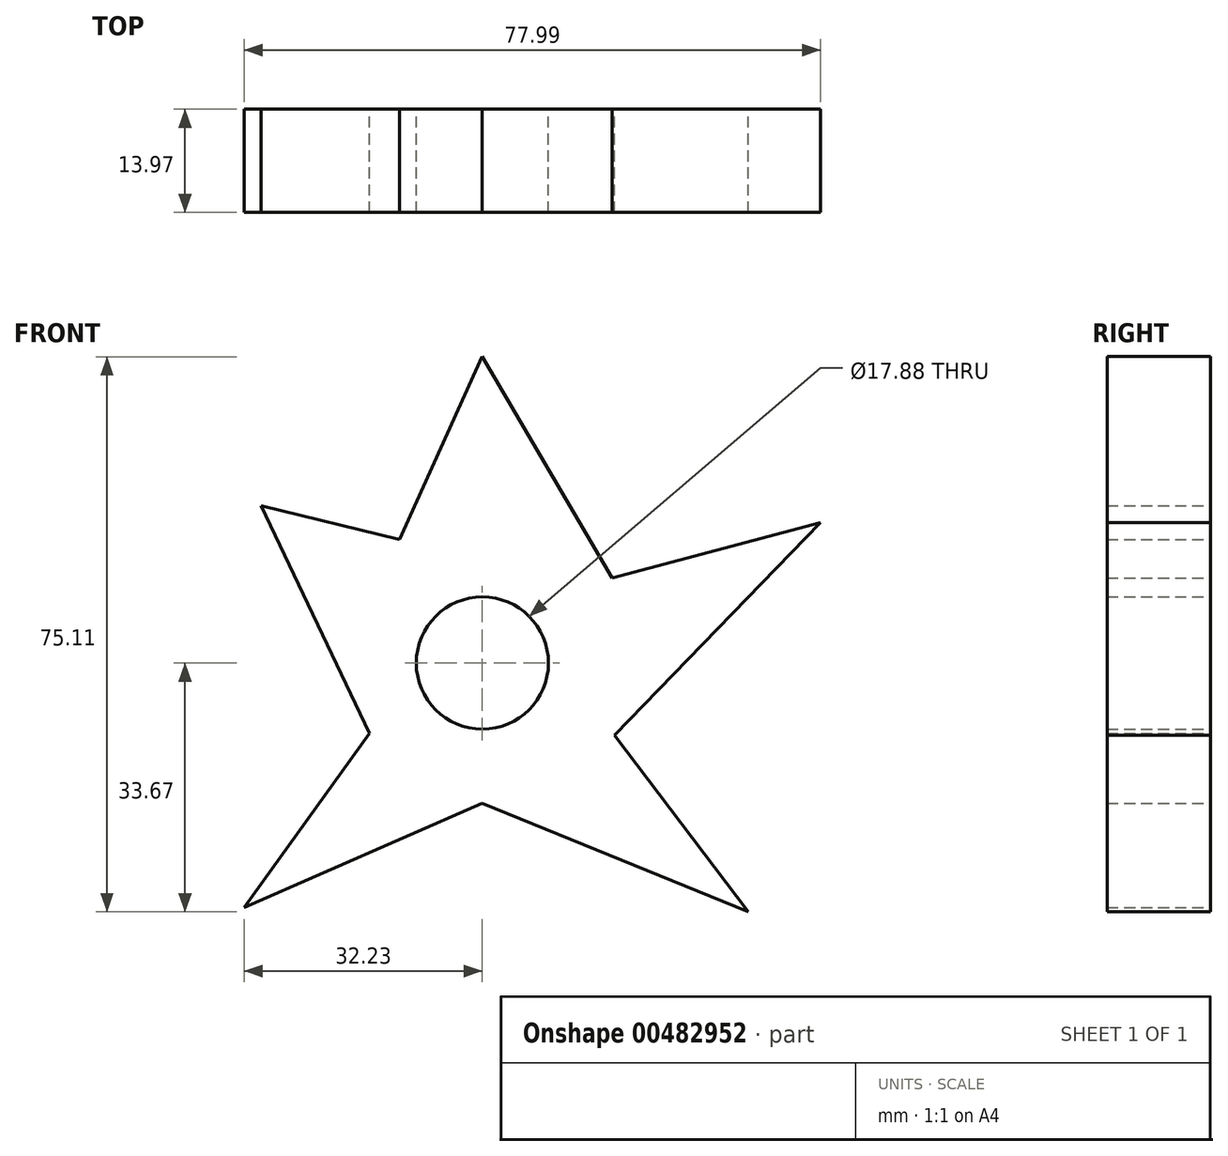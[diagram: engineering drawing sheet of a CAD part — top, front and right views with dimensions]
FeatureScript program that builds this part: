
annotation { "Feature Type Name" : "Feature", "Feature Type Description" : "" }
export const myFeature = defineFeature(function(context is Context, id is Id, definition is map)
    precondition{}
    {
        {
            var Q0;
            Q0=qCreatedBy(makeId("Front.planeOp"),FACE);
            var sketch = newSketch(context, id + "F0", { "sketchPlane" : qUnion([Q0])});
            skLineSegment(sketch, "E0", {"start": v(0, 41.44) * mm, "end": v(17.56, 11.51) * mm});
            skLineSegment(sketch, "E1", {"start": v(17.56, 11.51) * mm, "end": v(45.76, 19) * mm});
            skLineSegment(sketch, "E2", {"start": v(45.76, 19) * mm, "end": v(17.84, -9.79) * mm});
            skLineSegment(sketch, "E3", {"start": v(17.84, -9.79) * mm, "end": v(35.98, -33.67) * mm});
            skLineSegment(sketch, "E4", {"start": v(35.98, -33.67) * mm, "end": v(0, -19) * mm});
            skLineSegment(sketch, "E5", {"start": v(0, -19) * mm, "end": v(-32.23, -33.1) * mm});
            skLineSegment(sketch, "E6", {"start": v(-32.23, -33.1) * mm, "end": v(-15.25, -9.5) * mm});
            skLineSegment(sketch, "E7", {"start": v(-15.25, -9.5) * mm, "end": v(-29.93, 21.3) * mm});
            skLineSegment(sketch, "E8", {"start": v(-29.93, 21.3) * mm, "end": v(-11.22, 16.7) * mm});
            skLineSegment(sketch, "E9", {"start": v(-11.22, 16.7) * mm, "end": v(0, 41.44) * mm});
            skSolve(sketch);
        }
        {
            var Q0;
            Q0 = qSketchRegion(id + "F0", true);
            extrude(context, id + "F1", {"entities" : qUnion([Q0]), "depth" : 13.97 * mm});
        }
        {
            var Q0;
            Q0=qCreatedBy(makeId("Front.planeOp"),FACE);
            var sketch = newSketch(context, id + "F2", { "sketchPlane" : qUnion([Q0])});
            skCircle(sketch, "E10", {"center": v(0, 0) * mm, "radius": 8.94 * mm});
            skSolve(sketch);
        }
        {
            var Q0;
            Q0=makeQuery(id+"F2.imprint","IMPRINT",FACE,{"disambiguationData":[TD([[makeQuery(id+"F2.imprint","IMPRINT",EDGE,{"derivedFrom":sQuery(id+"F2.wireOp",EDGE,"E10")}),1.0]])]});
            var Q1;
            Q1=sQuery(id+"F2.wireOp",EDGE,"E10");
            extrude(context, id + "F3", {"entities" : qUnion([Q0]), "operationType" : NewBodyOperationType.REMOVE, "surfaceEntities" : qUnion([Q1]), "endBound" : BoundingType.UP_TO_NEXT, "depth" : 47 * mm});
        }
    });
